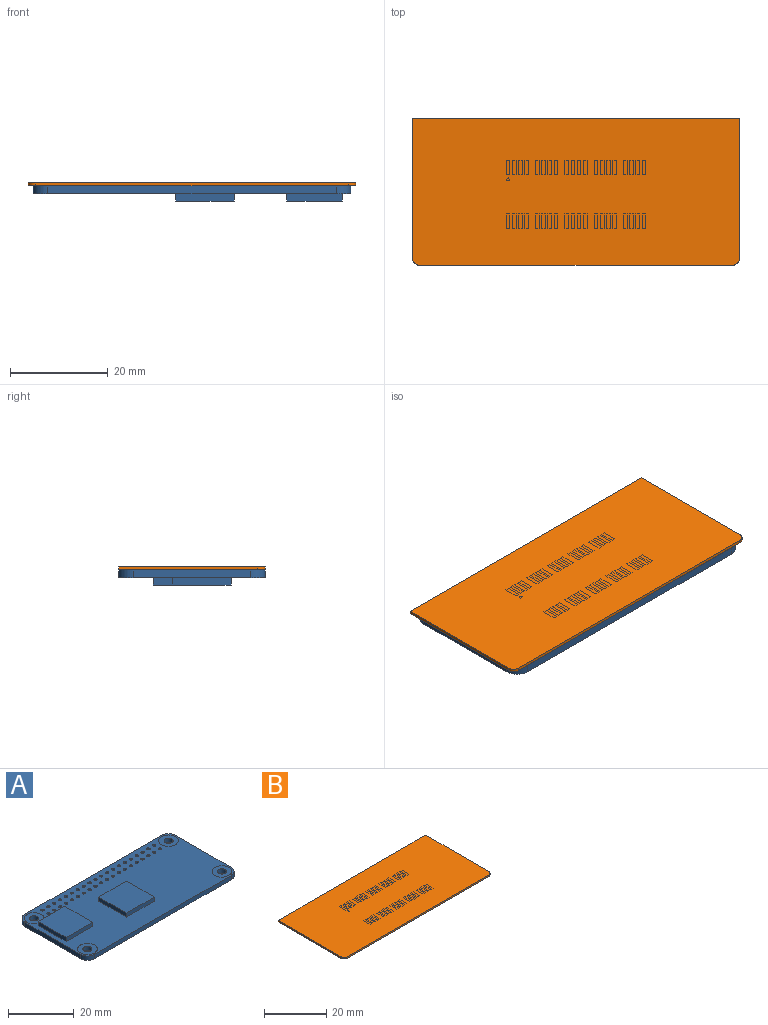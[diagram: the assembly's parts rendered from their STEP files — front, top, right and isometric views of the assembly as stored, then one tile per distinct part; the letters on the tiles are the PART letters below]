
ASSEMBLY  parts=2 mates=1
PART A: 88 faces, bbox 65x30x3.1 mm
  f0: plane 65x30mm, normal (0,0,-1), area 1823.4mm2, adj f1,f2,f3,f4,f5,f6,f7,f8
  f1: plane 2.05x2.05mm, normal (0,0,-1), area 3.3mm2, adj f0
  f2: plane 2.05x2.05mm, normal (0,0,-1), area 3.3mm2, adj f0
  f3: plane 2.05x2.05mm, normal (0,0,-1), area 3.3mm2, adj f0
  f4: plane 2.05x2.05mm, normal (0,0,-1), area 3.3mm2, adj f0
  f5: plane 2.05x2.05mm, normal (0,0,-1), area 3.3mm2, adj f0
  f6: plane 2.05x2.05mm, normal (0,0,-1), area 3.3mm2, adj f0
  f7: plane 2.05x2.05mm, normal (0,0,-1), area 3.3mm2, adj f0
  f8: plane 2.05x2.05mm, normal (0,0,-1), area 3.3mm2, adj f0
  f9: plane 2.05x2.05mm, normal (0,0,-1), area 3.3mm2, adj f0
  f10: plane 2.05x2.05mm, normal (0,0,-1), area 3.3mm2, adj f0
  f11: plane 2.05x2.05mm, normal (0,0,-1), area 3.3mm2, adj f0
  f12: plane 2.05x2.05mm, normal (0,0,-1), area 3.3mm2, adj f0
  f13: plane 2.05x2.05mm, normal (0,0,-1), area 3.3mm2, adj f0
  f14: plane 2.05x2.05mm, normal (0,0,-1), area 3.3mm2, adj f0
  f15: plane 2.05x2.05mm, normal (0,0,-1), area 3.3mm2, adj f0
  f16: plane 2.05x2.05mm, normal (0,0,-1), area 3.3mm2, adj f0
  f17: plane 1.65x1.65mm, normal (0,0,-1), area 2.1mm2, adj f0
  f18: plane 1.65x1.65mm, normal (0,0,-1), area 2.1mm2, adj f0
  f19: plane 2.05x2.05mm, normal (0,0,-1), area 3.3mm2, adj f0
  f20: plane 65x30mm, normal (0,0,1), area 1517mm2, adj f21,f22,f23,f24,f26,f27,f28,f29
  f21: plane 6x6mm, normal (0,0,1), area 22.3mm2, adj f20,f34
  f22: plane 6x6mm, normal (0,0,1), area 22.3mm2, adj f20,f35
  f23: plane 6x6mm, normal (0,0,1), area 22.3mm2, adj f20,f36
  f24: plane 6x6mm, normal (0,0,1), area 22.3mm2, adj f20,f37
  f25: plane 2.05x2.05mm, normal (0,0,-1), area 3.3mm2, adj f0
  f26: cylinder r=3mm len=3mm, axis (0,0,-1), area 7.5mm2, adj f0,f20,f27,f33
  f27: plane 24x1.6mm, normal (-1,0,0), area 38.4mm2, adj f0,f20,f26,f28
  f28: cylinder r=3mm len=3mm, axis (0,0,-1), area 7.5mm2, adj f0,f20,f27,f29
  f29: plane 59x1.6mm, normal (0,-1,0), area 94.4mm2, adj f0,f20,f28,f30
  f30: cylinder r=3mm len=3mm, axis (0,0,-1), area 7.5mm2, adj f0,f20,f29,f31
  f31: plane 24x1.6mm, normal (1,0,0), area 38.4mm2, adj f0,f20,f30,f32
  f32: cylinder r=3mm len=3mm, axis (0,0,-1), area 7.5mm2, adj f0,f20,f31,f33
  f33: plane 59x1.6mm, normal (0,1,0), area 94.4mm2, adj f0,f20,f26,f32
  f34: cylinder r=1.38mm len=2.75mm, axis (0,0,-1), area 13.8mm2, adj f0,f21
  f35: cylinder r=1.38mm len=2.75mm, axis (0,0,-1), area 13.8mm2, adj f0,f22
  f36: cylinder r=1.38mm len=2.75mm, axis (0,0,-1), area 13.8mm2, adj f0,f23
  f37: cylinder r=1.38mm len=2.75mm, axis (0,0,-1), area 13.8mm2, adj f0,f24
  f38: cylinder r=0.5mm len=1.6mm, axis (0,0,-1), area 5mm2, adj f0,f20
  f39: cylinder r=0.5mm len=1.6mm, axis (0,0,-1), area 5mm2, adj f0,f20
  f40: cylinder r=0.5mm len=1.6mm, axis (0,0,-1), area 5mm2, adj f0,f20
  f41: cylinder r=0.5mm len=1.6mm, axis (0,0,-1), area 5mm2, adj f0,f20
  f42: cylinder r=0.5mm len=1.6mm, axis (0,0,-1), area 5mm2, adj f0,f20
  f43: cylinder r=0.5mm len=1.6mm, axis (0,0,-1), area 5mm2, adj f0,f20
  f44: cylinder r=0.5mm len=1.6mm, axis (0,0,-1), area 5mm2, adj f0,f20
  f45: cylinder r=0.5mm len=1.6mm, axis (0,0,-1), area 5mm2, adj f0,f20
  f46: cylinder r=0.5mm len=1.6mm, axis (0,0,-1), area 5mm2, adj f0,f20
  f47: cylinder r=0.5mm len=1.6mm, axis (0,0,-1), area 5mm2, adj f0,f20
  f48: cylinder r=0.5mm len=1.6mm, axis (0,0,-1), area 5mm2, adj f0,f20
  f49: cylinder r=0.5mm len=1.6mm, axis (0,0,-1), area 5mm2, adj f0,f20
  f50: cylinder r=0.5mm len=1.6mm, axis (0,0,-1), area 5mm2, adj f0,f20
  f51: cylinder r=0.5mm len=1.6mm, axis (0,0,-1), area 5mm2, adj f0,f20
  f52: cylinder r=0.5mm len=1.6mm, axis (0,0,-1), area 5mm2, adj f0,f20
  f53: cylinder r=0.5mm len=1.6mm, axis (0,0,-1), area 5mm2, adj f0,f20
  f54: cylinder r=0.5mm len=1.6mm, axis (0,0,-1), area 5mm2, adj f0,f20
  f55: cylinder r=0.5mm len=1.6mm, axis (0,0,-1), area 5mm2, adj f0,f20
  f56: cylinder r=0.5mm len=1.6mm, axis (0,0,-1), area 5mm2, adj f0,f20
  f57: cylinder r=0.5mm len=1.6mm, axis (0,0,-1), area 5mm2, adj f0,f20
  f58: cylinder r=0.5mm len=1.6mm, axis (0,0,-1), area 5mm2, adj f0,f20
  f59: cylinder r=0.5mm len=1.6mm, axis (0,0,-1), area 5mm2, adj f0,f20
  f60: cylinder r=0.5mm len=1.6mm, axis (0,0,-1), area 5mm2, adj f0,f20
  f61: cylinder r=0.5mm len=1.6mm, axis (0,0,-1), area 5mm2, adj f0,f20
  f62: cylinder r=0.5mm len=1.6mm, axis (0,0,-1), area 5mm2, adj f0,f20
  f63: cylinder r=0.5mm len=1.6mm, axis (0,0,-1), area 5mm2, adj f0,f20
  f64: cylinder r=0.5mm len=1.6mm, axis (0,0,-1), area 5mm2, adj f0,f20
  f65: cylinder r=0.5mm len=1.6mm, axis (0,0,-1), area 5mm2, adj f0,f20
  f66: cylinder r=0.5mm len=1.6mm, axis (0,0,-1), area 5mm2, adj f0,f20
  f67: cylinder r=0.5mm len=1.6mm, axis (0,0,-1), area 5mm2, adj f0,f20
  f68: cylinder r=0.5mm len=1.6mm, axis (0,0,-1), area 5mm2, adj f0,f20
  f69: cylinder r=0.5mm len=1.6mm, axis (0,0,-1), area 5mm2, adj f0,f20
  f70: cylinder r=0.5mm len=1.6mm, axis (0,0,-1), area 5mm2, adj f0,f20
  f71: cylinder r=0.5mm len=1.6mm, axis (0,0,-1), area 5mm2, adj f0,f20
  f72: cylinder r=0.5mm len=1.6mm, axis (0,0,-1), area 5mm2, adj f0,f20
  f73: cylinder r=0.5mm len=1.6mm, axis (0,0,-1), area 5mm2, adj f0,f20
  f74: cylinder r=0.5mm len=1.6mm, axis (0,0,-1), area 5mm2, adj f0,f20
  f75: cylinder r=0.5mm len=1.6mm, axis (0,0,-1), area 5mm2, adj f0,f20
  f76: cylinder r=0.5mm len=1.6mm, axis (0,0,-1), area 5mm2, adj f0,f20
  f77: cylinder r=0.5mm len=1.6mm, axis (0,0,-1), area 5mm2, adj f0,f20
  f78: plane 12x1.5mm, normal (-1,0,0), area 18mm2, adj f20,f79,f81,f82
  f79: plane 12x1.5mm, normal (0,-1,0), area 18mm2, adj f20,f78,f80,f82
  f80: plane 12x1.5mm, normal (1,0,0), area 18mm2, adj f20,f79,f81,f82
  f81: plane 12x1.5mm, normal (0,1,0), area 18mm2, adj f20,f78,f80,f82
  f82: plane 12x12mm, normal (0,0,1), area 144mm2, adj f78,f79,f80,f81
  f83: plane 12x1.5mm, normal (1,0,0), area 18mm2, adj f20,f84,f86,f87
  f84: plane 11.4x1.5mm, normal (0,1,0), area 17.1mm2, adj f20,f83,f85,f87
  f85: plane 12x1.5mm, normal (-1,0,0), area 18mm2, adj f20,f84,f86,f87
  f86: plane 11.4x1.5mm, normal (0,-1,0), area 17.1mm2, adj f20,f83,f85,f87
  f87: plane 12x11.4mm, normal (0,0,1), area 136.8mm2, adj f83,f84,f85,f86
PART B: 49 faces, bbox 67x30x0.6 mm
  f0: plane 0.75x0.65mm, normal (0,0,1), area 0.2mm2, adj f2
  f1: plane 3x0.75mm, normal (0,0,1), area 2.2mm2, adj f2
  f2: plane 67x30mm, normal (0,0,1), area 1918.8mm2, adj f0,f1,f3,f4,f5,f6,f7,f8
  f3: plane 3x0.75mm, normal (0,0,1), area 2.3mm2, adj f2
  f4: plane 3x0.75mm, normal (0,0,1), area 2.3mm2, adj f2
  f5: plane 3x0.75mm, normal (0,0,1), area 2.2mm2, adj f2
  f6: plane 3x0.75mm, normal (0,0,1), area 2.3mm2, adj f2
  f7: plane 3x0.75mm, normal (0,0,1), area 2.3mm2, adj f2
  f8: plane 3x0.75mm, normal (0,0,1), area 2.3mm2, adj f2
  f9: plane 3x0.75mm, normal (0,0,1), area 2.2mm2, adj f2
  f10: plane 3x0.75mm, normal (0,0,1), area 2.3mm2, adj f2
  f11: plane 3x0.75mm, normal (0,0,1), area 2.3mm2, adj f2
  f12: plane 3x0.75mm, normal (0,0,1), area 2.2mm2, adj f2
  f13: plane 3x0.75mm, normal (0,0,1), area 2.2mm2, adj f2
  f14: plane 3x0.75mm, normal (0,0,1), area 2.2mm2, adj f2
  f15: plane 3x0.75mm, normal (0,0,1), area 2.3mm2, adj f2
  f16: plane 3x0.75mm, normal (0,0,1), area 2.2mm2, adj f2
  f17: plane 3x0.75mm, normal (0,0,1), area 2.3mm2, adj f2
  f18: plane 3x0.75mm, normal (0,0,1), area 2.2mm2, adj f2
  f19: plane 3x0.75mm, normal (0,0,1), area 2.3mm2, adj f2
  f20: plane 3x0.75mm, normal (0,0,1), area 2.3mm2, adj f2
  f21: plane 3x0.75mm, normal (0,0,1), area 2.2mm2, adj f2
  f22: plane 3x0.75mm, normal (0,0,1), area 2.3mm2, adj f2
  f23: plane 3x0.75mm, normal (0,0,1), area 2.2mm2, adj f2
  f24: plane 3x0.75mm, normal (0,0,1), area 2.2mm2, adj f2
  f25: plane 3x0.75mm, normal (0,0,1), area 2.2mm2, adj f2
  f26: plane 3x0.75mm, normal (0,0,1), area 2.2mm2, adj f2
  f27: plane 3x0.75mm, normal (0,0,1), area 2.2mm2, adj f2
  f28: plane 3x0.75mm, normal (0,0,1), area 2.3mm2, adj f2
  f29: plane 3x0.75mm, normal (0,0,1), area 2.2mm2, adj f2
  f30: plane 3x0.75mm, normal (0,0,1), area 2.2mm2, adj f2
  f31: plane 3x0.75mm, normal (0,0,1), area 2.2mm2, adj f2
  f32: plane 3x0.75mm, normal (0,0,1), area 2.3mm2, adj f2
  f33: plane 3x0.75mm, normal (0,0,1), area 2.3mm2, adj f2
  f34: plane 3x0.75mm, normal (0,0,1), area 2.2mm2, adj f2
  f35: plane 3x0.75mm, normal (0,0,1), area 2.3mm2, adj f2
  f36: plane 3x0.75mm, normal (0,0,1), area 2.3mm2, adj f2
  f37: plane 3x0.75mm, normal (0,0,1), area 2.3mm2, adj f2
  f38: plane 3x0.75mm, normal (0,0,1), area 2.3mm2, adj f2
  f39: plane 3x0.75mm, normal (0,0,1), area 2.3mm2, adj f2
  f40: plane 3x0.75mm, normal (0,0,1), area 2.2mm2, adj f2
  f41: plane 3x0.75mm, normal (0,0,1), area 2.2mm2, adj f2
  f42: cylinder r=1.5mm len=1.5mm, axis (0,0,-1), area 1.4mm2, adj f2,f43,f45,f47
  f43: plane 64x0.6mm, normal (0,-1,0), area 38.4mm2, adj f2,f42,f44,f45
  f44: cylinder r=1.5mm len=1.5mm, axis (0,0,-1), area 1.4mm2, adj f2,f43,f45,f46
  f45: plane 67x30mm, normal (0,0,-1), area 2009mm2, adj f42,f43,f44,f46,f47,f48
  f46: plane 28.5x0.6mm, normal (1,0,0), area 17.1mm2, adj f2,f44,f45,f48
  f47: plane 28.5x0.6mm, normal (-1,0,0), area 17.1mm2, adj f2,f42,f45,f48
  f48: plane 67x0.6mm, normal (0,1,0), area 40.2mm2, adj f2,f45,f46,f47
PLACE A rot(axis=(0,1,0),180deg) t=(0,22.56,4.7)mm
PLACE B at identity
MATE fastened A.f0 <-> B.f45  axis (0,0,1) through (0,22.56,4.7)mm
